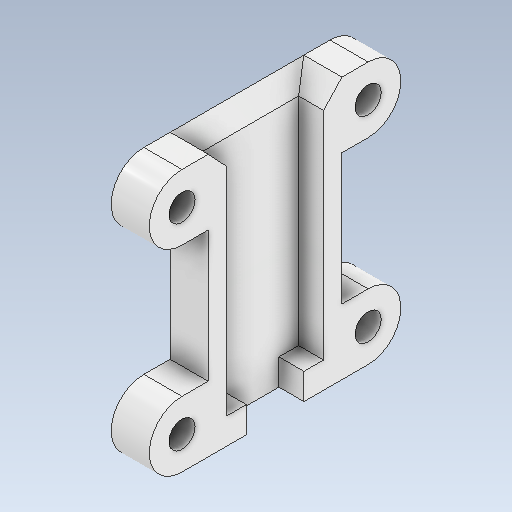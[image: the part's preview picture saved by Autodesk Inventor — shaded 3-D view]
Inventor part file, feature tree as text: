
AUTODESK INVENTOR PART (.ipt)
format: ipt  version: 2020 (Build 240168000, 168)  size: 180,736 bytes
history: native  units: in
note: dims shown in document units (in); Inventor stores cm internally (conversion verified against a paired STEP export)
features: sketch x6, other x3
ambient origin geometry x8: Origin, YZ Plane, XZ Plane, XY Plane, X Axis, Y Axis, Z Axis, Center Point
bodies: Solid1 (feature_tree)
feature tree (9):
  other  "PistonCasingTop.ipt"
  other  "Solid1::PistonCasingTop.ipt"
  other  "TaggingFeature1"
  sketch  "Sketch1"  dims[d0=0.3937in]
  sketch  "Sketch2"
  sketch  "Sketch3"
  sketch  "Sketch4"
  sketch  "Sketch5"
  sketch  "Sketch6"
